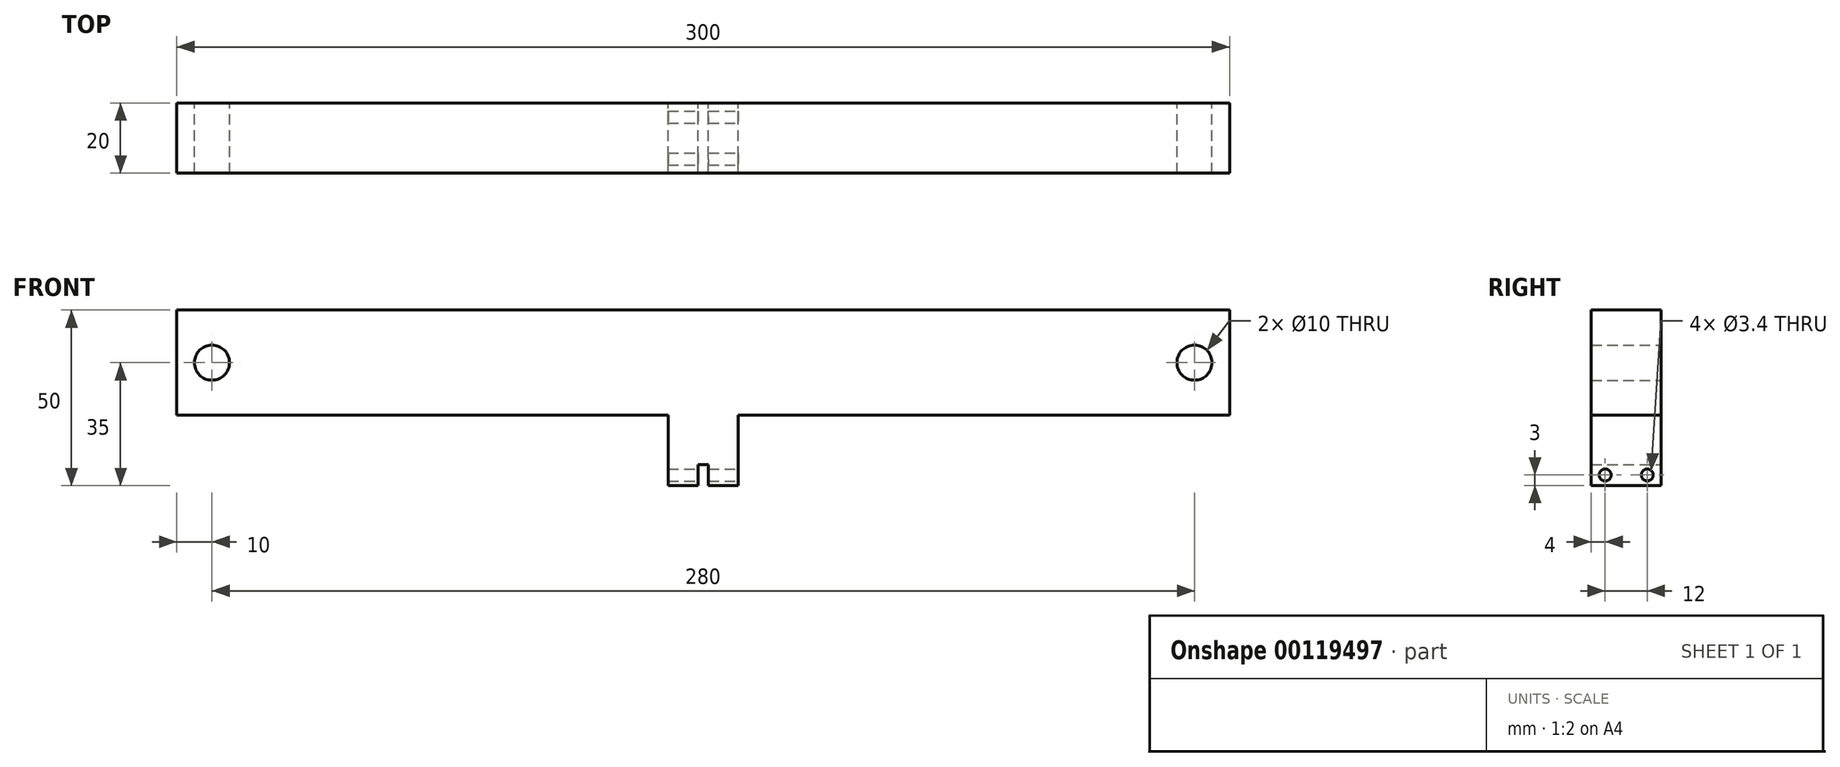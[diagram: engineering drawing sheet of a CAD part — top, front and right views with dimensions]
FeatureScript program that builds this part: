
annotation { "Feature Type Name" : "Feature", "Feature Type Description" : "" }
export const myFeature = defineFeature(function(context is Context, id is Id, definition is map)
    precondition{}
    {
        {
            var Q0;
            Q0=qCreatedBy(makeId("Front.planeOp"),FACE);
            var sketch = newSketch(context, id + "F0", { "sketchPlane" : qUnion([Q0])});
            skLineSegment(sketch, "E0.bottom", {"start": v(150, -15) * mm, "end": v(-150, -15) * mm});
            skLineSegment(sketch, "E0.top", {"start": v(150, 15) * mm, "end": v(-150, 15) * mm});
            skLineSegment(sketch, "E0.left", {"start": v(150, -15) * mm, "end": v(150, 15) * mm});
            skLineSegment(sketch, "E0.right", {"start": v(-150, -15) * mm, "end": v(-150, 15) * mm});
            skPoint(sketch, "E0.middle", {"position": v(0, 0) * mm});
            skLineSegment(sketch, "E1.bottom", {"start": v(10, -35) * mm, "end": v(1.5, -35) * mm});
            skLineSegment(sketch, "E1.top", {"start": v(10, 5) * mm, "end": v(-10, 5) * mm});
            skLineSegment(sketch, "E1.left", {"start": v(10, -35) * mm, "end": v(10, 5) * mm});
            skLineSegment(sketch, "E1.right", {"start": v(-10, -35) * mm, "end": v(-10, 5) * mm});
            skPoint(sketch, "E1.middle", {"position": v(0, -15) * mm});
            skLineSegment(sketch, "E2.top", {"start": v(1.5, -29) * mm, "end": v(-1.5, -29) * mm});
            skLineSegment(sketch, "E2.left", {"start": v(1.5, -35) * mm, "end": v(1.5, -29) * mm});
            skLineSegment(sketch, "E2.right", {"start": v(-1.5, -35) * mm, "end": v(-1.5, -29) * mm});
            skPoint(sketch, "E2.middle", {"position": v(0, -35) * mm});
            skLineSegment(sketch, "E3.trimOffspring", {"start": v(-1.5, -35) * mm, "end": v(-10, -35) * mm});
            skPoint(sketch, "E2.bottom.end.orphan", {"position": v(-1.5, -41) * mm});
            skPoint(sketch, "E2.bottom.start.orphan", {"position": v(1.5, -41) * mm});
            skCircle(sketch, "E4", {"center": v(-140, 0) * mm, "radius": 5 * mm});
            skCircle(sketch, "E5.MirrorC", {"center": v(140, 0) * mm, "radius": 5 * mm});
            skSolve(sketch);
        }
        {
            var Q0;
            Q0 = qSketchRegion(id + "F0", true);
            extrude(context, id + "F1", {"entities" : qUnion([Q0]), "depth" : 10 * mm, "hasSecondDirection" : true, "secondDirectionOppositeDirection" : true, "secondDirectionDepth" : 10 * mm});
        }
        {
            var Q0;
            Q0=makeQuery(id+"F1.opExtrude","SWEPT_FACE",FACE,{"disambiguationData":[OSD([sQuery(id+"F0.wireOp",EDGE,"E1.left")])]});
            var sketch = newSketch(context, id + "F2", { "sketchPlane" : qUnion([Q0])});
            skCircle(sketch, "E6", {"center": v(-6, -32) * mm, "radius": 1.7 * mm});
            skCircle(sketch, "E7.MirrorC", {"center": v(6, -32) * mm, "radius": 1.7 * mm});
            skSolve(sketch);
        }
        {
            var Q0;
            Q0 = qSketchRegion(id + "F2", true);
            extrude(context, id + "F3", {"entities" : qUnion([Q0]), "operationType" : NewBodyOperationType.REMOVE, "oppositeDirection" : true, "depth" : 25 * mm});
        }
    });
